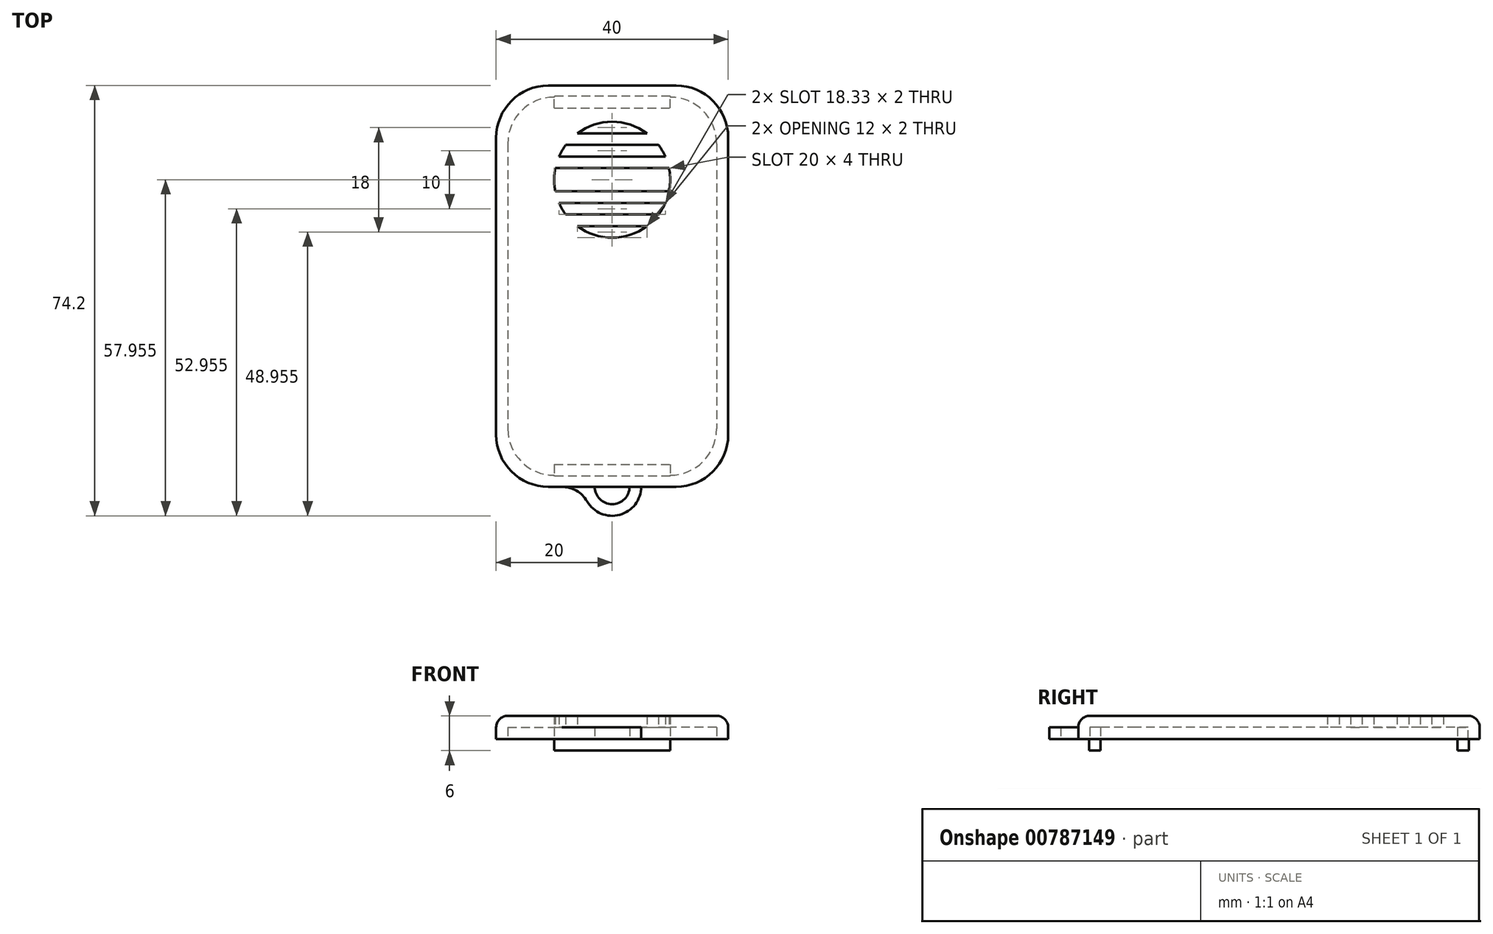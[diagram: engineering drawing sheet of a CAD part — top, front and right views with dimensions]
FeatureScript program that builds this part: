
annotation { "Feature Type Name" : "Feature", "Feature Type Description" : "" }
export const myFeature = defineFeature(function(context is Context, id is Id, definition is map)
    precondition{}
    {
        {
            var Q0;
            Q0=qCreatedBy(makeId("Top.planeOp"),FACE);
            var sketch = newSketch(context, id + "F0", { "sketchPlane" : qUnion([Q0])});
            skLineSegment(sketch, "E0.bottom", {"start": v(-18, 33) * mm, "end": v(18, 33) * mm});
            skLineSegment(sketch, "E0.top", {"start": v(-18, -32.2) * mm, "end": v(18, -32.2) * mm});
            skLineSegment(sketch, "E0.left", {"start": v(-18, 33) * mm, "end": v(-18, -32.2) * mm});
            skLineSegment(sketch, "E0.right", {"start": v(18, 33) * mm, "end": v(18, -32.2) * mm});
            skLineSegment(sketch, "E1.0", {"start": v(20, 35) * mm, "end": v(20, -34.2) * mm});
            skLineSegment(sketch, "E1.1", {"start": v(-20, 35) * mm, "end": v(20, 35) * mm});
            skLineSegment(sketch, "E1.2", {"start": v(-20, 35) * mm, "end": v(-20, -34.2) * mm});
            skLineSegment(sketch, "E1.3", {"start": v(-20, -34.2) * mm, "end": v(20, -34.2) * mm});
            skSolve(sketch);
        }
        {
            var Q0;
            Q0 = qSketchRegion(id + "F0", true);
            extrude(context, id + "F1", {"entities" : qUnion([Q0]), "depth" : 2 * mm, "offsetDistance" : 25 * mm});
        }
        {
            var Q0;
            Q0=qCreatedBy(makeId("Top.planeOp"),FACE);
            var sketch = newSketch(context, id + "F2", { "sketchPlane" : qUnion([Q0])});
            skLineSegment(sketch, "E2.bottom", {"start": v(-10, -30.35) * mm, "end": v(10, -30.35) * mm});
            skLineSegment(sketch, "E2.top", {"start": v(-10, -32.35) * mm, "end": v(10, -32.35) * mm});
            skLineSegment(sketch, "E2.left", {"start": v(-10, -30.35) * mm, "end": v(-10, -32.35) * mm});
            skLineSegment(sketch, "E2.right", {"start": v(10, -30.35) * mm, "end": v(10, -32.35) * mm});
            skLineSegment(sketch, "E3.bottom", {"start": v(-10, 31.15) * mm, "end": v(10, 31.15) * mm});
            skLineSegment(sketch, "E3.top", {"start": v(-10, 33.15) * mm, "end": v(10, 33.15) * mm});
            skLineSegment(sketch, "E3.left", {"start": v(-10, 31.15) * mm, "end": v(-10, 33.15) * mm});
            skLineSegment(sketch, "E3.right", {"start": v(10, 31.15) * mm, "end": v(10, 33.15) * mm});
            skSolve(sketch);
        }
        {
            var Q0;
            Q0 = qSketchRegion(id + "F2", true);
            extrude(context, id + "F3", {"entities" : qUnion([Q0]), "operationType" : NewBodyOperationType.ADD, "endBound" : BoundingType.SYMMETRIC, "depth" : 4 * mm, "offsetDistance" : 25 * mm});
        }
        {
            var Q0;
            Q0=makeQuery(id+"F3.boolean.opBoolean","MERGE",FACE,{"derivedFrom":[makeQuery(id+"F1.opExtrude","CAP_FACE",FACE,{"disambiguationData":[OSD([sQuery(id+"F0.wireOp",EDGE,"E0.bottom"),sQuery(id+"F0.wireOp",EDGE,"E0.top"),sQuery(id+"F0.wireOp",EDGE,"E0.left"),sQuery(id+"F0.wireOp",EDGE,"E0.right"),sQuery(id+"F0.wireOp",EDGE,"E1.0"),sQuery(id+"F0.wireOp",EDGE,"E1.1"),sQuery(id+"F0.wireOp",EDGE,"E1.2"),sQuery(id+"F0.wireOp",EDGE,"E1.3")])],"isStart":false}),makeQuery(id+"F3.opExtrude","CAP_FACE",FACE,{"disambiguationData":[OSD([sQuery(id+"F2.wireOp",EDGE,"E2.bottom"),sQuery(id+"F2.wireOp",EDGE,"E2.top"),sQuery(id+"F2.wireOp",EDGE,"E2.left"),sQuery(id+"F2.wireOp",EDGE,"E2.right")])],"isStart":false}),makeQuery(id+"F3.opExtrude","CAP_FACE",FACE,{"disambiguationData":[OSD([sQuery(id+"F2.wireOp",EDGE,"E3.bottom"),sQuery(id+"F2.wireOp",EDGE,"E3.top"),sQuery(id+"F2.wireOp",EDGE,"E3.left"),sQuery(id+"F2.wireOp",EDGE,"E3.right")])],"isStart":false})]});
            var sketch = newSketch(context, id + "F4", { "sketchPlane" : qUnion([Q0])});
            skLineSegment(sketch, "E4.bottom", {"start": v(-20, 35) * mm, "end": v(20, 35) * mm});
            skLineSegment(sketch, "E4.top", {"start": v(-20, -34.2) * mm, "end": v(20, -34.2) * mm});
            skLineSegment(sketch, "E4.left", {"start": v(-20, 35) * mm, "end": v(-20, -34.2) * mm});
            skLineSegment(sketch, "E4.right", {"start": v(20, 35) * mm, "end": v(20, -34.2) * mm});
            skArc(sketch, "E5", {"start": v(-6, 10.76) * mm, "mid": v(0, 8.76) * mm, "end": v(6, 10.76) * mm});
            skLineSegment(sketch, "E6.1.0.0", {"start": v(-9.8, 16.76) * mm, "end": v(9.8, 16.76) * mm});
            skLineSegment(sketch, "E6.2.0.0", {"start": v(-9.17, 14.76) * mm, "end": v(9.17, 14.76) * mm});
            skLineSegment(sketch, "E7.0.3.0", {"start": v(-8, 12.76) * mm, "end": v(8, 12.76) * mm});
            skLineSegment(sketch, "E8.0.4.0", {"start": v(-6, 10.76) * mm, "end": v(6, 10.76) * mm});
            skArc(sketch, "E9.trimOffspring", {"start": v(8, 12.76) * mm, "mid": v(8.64, 13.72) * mm, "end": v(9.17, 14.76) * mm});
            skArc(sketch, "E10.trimOffspring", {"start": v(-9.17, 14.76) * mm, "mid": v(-8.64, 13.72) * mm, "end": v(-8, 12.76) * mm});
            skArc(sketch, "E11.trimOffspring", {"start": v(9.8, 16.76) * mm, "mid": v(10, 18.76) * mm, "end": v(9.8, 20.76) * mm});
            skLineSegment(sketch, "E12.0", {"start": v(-9.8, 20.76) * mm, "end": v(9.8, 20.76) * mm});
            skLineSegment(sketch, "E13.0", {"start": v(-9.17, 22.76) * mm, "end": v(9.17, 22.76) * mm});
            skLineSegment(sketch, "E14.0", {"start": v(-8, 24.76) * mm, "end": v(8, 24.76) * mm});
            skLineSegment(sketch, "E15.0", {"start": v(-6, 26.76) * mm, "end": v(6, 26.76) * mm});
            skArc(sketch, "E16.trimOffspring", {"start": v(6, 26.76) * mm, "mid": v(0, 28.76) * mm, "end": v(-6, 26.76) * mm});
            skArc(sketch, "E17.trimOffspring", {"start": v(-8, 24.76) * mm, "mid": v(-8.64, 23.79) * mm, "end": v(-9.17, 22.76) * mm});
            skArc(sketch, "E18.trimOffspring", {"start": v(-9.8, 20.76) * mm, "mid": v(-10, 18.76) * mm, "end": v(-9.8, 16.76) * mm});
            skArc(sketch, "E19.trimOffspring", {"start": v(9.17, 22.76) * mm, "mid": v(8.64, 23.79) * mm, "end": v(8, 24.76) * mm});
            skPoint(sketch, "E20.orphan", {"position": v(-10, 18.76) * mm});
            skSolve(sketch);
        }
        {
            var Q0;
            Q0 = qSketchRegion(id + "F4", true);
            extrude(context, id + "F5", {"entities" : qUnion([Q0]), "operationType" : NewBodyOperationType.ADD, "depth" : 2 * mm, "offsetDistance" : 25 * mm});
        }
        {
            var Q0;
            Q0=makeQuery(id+"F1.opExtrude","SWEPT_EDGE",EDGE,{"disambiguationData":[OSD([sQuery(id+"F0.wireOp",EDGE,"E0.bottom"),sQuery(id+"F0.wireOp",EDGE,"E0.right")])]});
            var Q1;
            Q1=makeQuery(id+"F1.opExtrude","SWEPT_EDGE",EDGE,{"disambiguationData":[OSD([sQuery(id+"F0.wireOp",EDGE,"E0.bottom"),sQuery(id+"F0.wireOp",EDGE,"E0.left")])]});
            var Q2;
            Q2=makeQuery(id+"F1.opExtrude","SWEPT_EDGE",EDGE,{"disambiguationData":[OSD([sQuery(id+"F0.wireOp",EDGE,"E0.top"),sQuery(id+"F0.wireOp",EDGE,"E0.right")])]});
            var Q3;
            Q3=makeQuery(id+"F1.opExtrude","SWEPT_EDGE",EDGE,{"disambiguationData":[OSD([sQuery(id+"F0.wireOp",EDGE,"E0.top"),sQuery(id+"F0.wireOp",EDGE,"E0.left")])]});
            fillet(context, id + "F6", {"entities" : qUnion([Q0, Q1, Q2, Q3]), "radius" : 8 * mm, "tangentPropagation" : true, "allowEdgeOverflow" : false});
        }
        {
            var Q0;
            Q0=makeQuery(id+"F5.boolean.opBoolean","MERGE",EDGE,{"derivedFrom":[makeQuery(id+"F1.opExtrude","SWEPT_EDGE",EDGE,{"disambiguationData":[OSD([sQuery(id+"F0.wireOp",EDGE,"E1.2"),sQuery(id+"F0.wireOp",EDGE,"E1.3")])]}),makeQuery(id+"F5.opExtrude","SWEPT_EDGE",EDGE,{"disambiguationData":[OSD([sQuery(id+"F4.wireOp",EDGE,"E4.top"),sQuery(id+"F4.wireOp",EDGE,"E4.left")])]})]});
            var Q1;
            Q1=makeQuery(id+"F5.boolean.opBoolean","MERGE",EDGE,{"derivedFrom":[makeQuery(id+"F1.opExtrude","SWEPT_EDGE",EDGE,{"disambiguationData":[OSD([sQuery(id+"F0.wireOp",EDGE,"E1.1"),sQuery(id+"F0.wireOp",EDGE,"E1.2")])]}),makeQuery(id+"F5.opExtrude","SWEPT_EDGE",EDGE,{"disambiguationData":[OSD([sQuery(id+"F4.wireOp",EDGE,"E4.bottom"),sQuery(id+"F4.wireOp",EDGE,"E4.left")])]})]});
            var Q2;
            Q2=makeQuery(id+"F5.boolean.opBoolean","MERGE",EDGE,{"derivedFrom":[makeQuery(id+"F1.opExtrude","SWEPT_EDGE",EDGE,{"disambiguationData":[OSD([sQuery(id+"F0.wireOp",EDGE,"E1.0"),sQuery(id+"F0.wireOp",EDGE,"E1.1")])]}),makeQuery(id+"F5.opExtrude","SWEPT_EDGE",EDGE,{"disambiguationData":[OSD([sQuery(id+"F4.wireOp",EDGE,"E4.bottom"),sQuery(id+"F4.wireOp",EDGE,"E4.right")])]})]});
            var Q3;
            Q3=makeQuery(id+"F5.boolean.opBoolean","MERGE",EDGE,{"derivedFrom":[makeQuery(id+"F1.opExtrude","SWEPT_EDGE",EDGE,{"disambiguationData":[OSD([sQuery(id+"F0.wireOp",EDGE,"E1.0"),sQuery(id+"F0.wireOp",EDGE,"E1.3")])]}),makeQuery(id+"F5.opExtrude","SWEPT_EDGE",EDGE,{"disambiguationData":[OSD([sQuery(id+"F4.wireOp",EDGE,"E4.top"),sQuery(id+"F4.wireOp",EDGE,"E4.right")])]})]});
            fillet(context, id + "F7", {"entities" : qUnion([Q0, Q1, Q2, Q3]), "radius" : 9 * mm, "tangentPropagation" : true, "allowEdgeOverflow" : false});
        }
        {
            var Q0;
            Q0=makeQuery(id+"F5.opExtrude","CAP_EDGE",EDGE,{"disambiguationData":[OSD([sQuery(id+"F4.wireOp",EDGE,"E4.right")])],"isStart":false});
            fillet(context, id + "F8", {"entities" : qUnion([Q0]), "radius" : 2 * mm, "tangentPropagation" : true, "allowEdgeOverflow" : false});
        }
        {
            var Q0;
            Q0=makeQuery(id+"F1.opExtrude","CAP_FACE",FACE,{"disambiguationData":[OSD([sQuery(id+"F0.wireOp",EDGE,"E0.bottom"),sQuery(id+"F0.wireOp",EDGE,"E0.top"),sQuery(id+"F0.wireOp",EDGE,"E0.left"),sQuery(id+"F0.wireOp",EDGE,"E0.right"),sQuery(id+"F0.wireOp",EDGE,"E1.0"),sQuery(id+"F0.wireOp",EDGE,"E1.1"),sQuery(id+"F0.wireOp",EDGE,"E1.2"),sQuery(id+"F0.wireOp",EDGE,"E1.3")])],"isStart":true});
            var sketch = newSketch(context, id + "F9", { "sketchPlane" : qUnion([Q0])});
            skArc(sketch, "E21", {"start": v(5, 34.2) * mm, "mid": v(0, 39.2) * mm, "end": v(-5, 34.2) * mm});
            skArc(sketch, "E22", {"start": v(3, 34.2) * mm, "mid": v(0, 37.2) * mm, "end": v(-3, 34.2) * mm});
            skLineSegment(sketch, "E23", {"start": v(-5, 34.2) * mm, "end": v(-3, 34.2) * mm});
            skLineSegment(sketch, "E24", {"start": v(3, 34.2) * mm, "end": v(5, 34.2) * mm});
            skSolve(sketch);
        }
        {
            var Q0;
            Q0 = qSketchRegion(id + "F9", true);
            extrude(context, id + "F10", {"entities" : qUnion([Q0]), "operationType" : NewBodyOperationType.ADD, "oppositeDirection" : true, "depth" : 2 * mm, "offsetDistance" : 25 * mm});
        }
        {
            var Q0;
            Q0=makeQuery(id+"F10.opExtrude","SWEPT_EDGE",EDGE,{"disambiguationData":[OSD([sQuery(id+"F0.wireOp",EDGE,"E1.3"),sQuery(id+"F9.wireOp",EDGE,"E21"),sQuery(id+"F9.wireOp",EDGE,"E23")])]});
            var Q1;
            Q1=makeQuery(id+"F10.opExtrude","SWEPT_EDGE",EDGE,{"disambiguationData":[OSD([sQuery(id+"F0.wireOp",EDGE,"E1.3"),sQuery(id+"F9.wireOp",EDGE,"E21"),sQuery(id+"F9.wireOp",EDGE,"E24")])]});
            fillet(context, id + "F11", {"entities" : qUnion([Q0, Q1]), "radius" : 5 * mm, "tangentPropagation" : true, "allowEdgeOverflow" : false});
        }
    });
